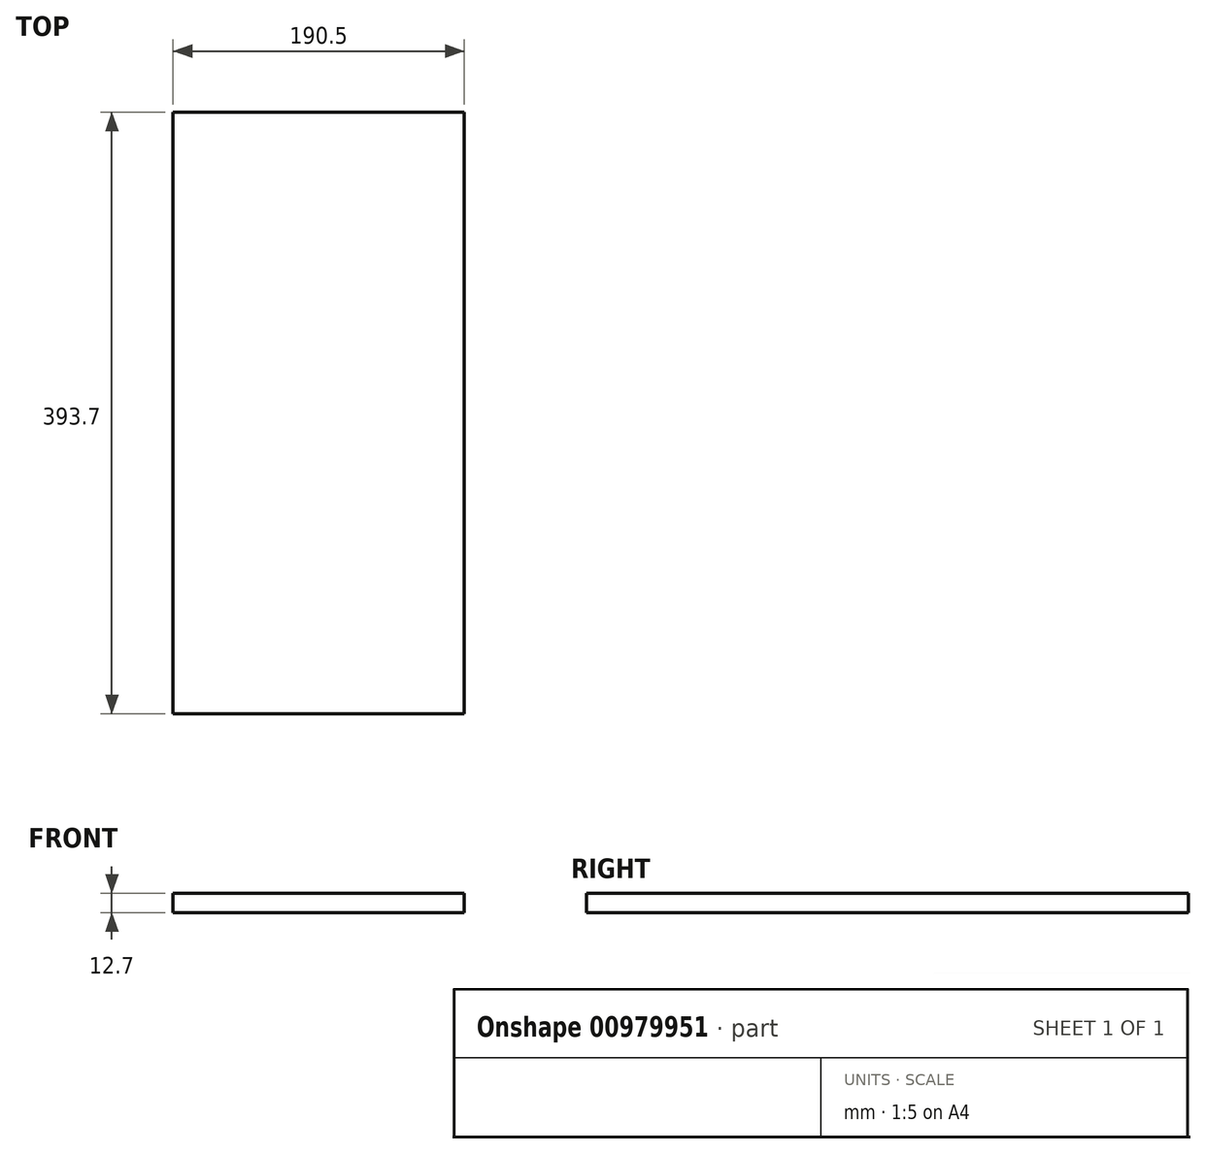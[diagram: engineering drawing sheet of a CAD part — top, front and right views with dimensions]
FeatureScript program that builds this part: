
annotation { "Feature Type Name" : "Feature", "Feature Type Description" : "" }
export const myFeature = defineFeature(function(context is Context, id is Id, definition is map)
    precondition{}
    {
        {
            var Q0;
            Q0=qCreatedBy(makeId("Top.planeOp"),FACE);
            var sketch = newSketch(context, id + "F0", { "sketchPlane" : qUnion([Q0])});
            skLineSegment(sketch, "E0.bottom", {"start": v(-95.25, 196.85) * mm, "end": v(95.25, 196.85) * mm});
            skLineSegment(sketch, "E0.top", {"start": v(-95.25, -196.85) * mm, "end": v(95.25, -196.85) * mm});
            skLineSegment(sketch, "E0.left", {"start": v(-95.25, 196.85) * mm, "end": v(-95.25, -196.85) * mm});
            skLineSegment(sketch, "E0.right", {"start": v(95.25, 196.85) * mm, "end": v(95.25, -196.85) * mm});
            skSolve(sketch);
        }
        {
            var Q0;
            Q0=qSketchRegion(id+"F0",true);
            extrude(context, id + "F1", {"entities" : qUnion([Q0]), "oppositeDirection" : true, "depth" : 12.7 * mm, "offsetDistance" : 25.4 * mm});
        }
    });
